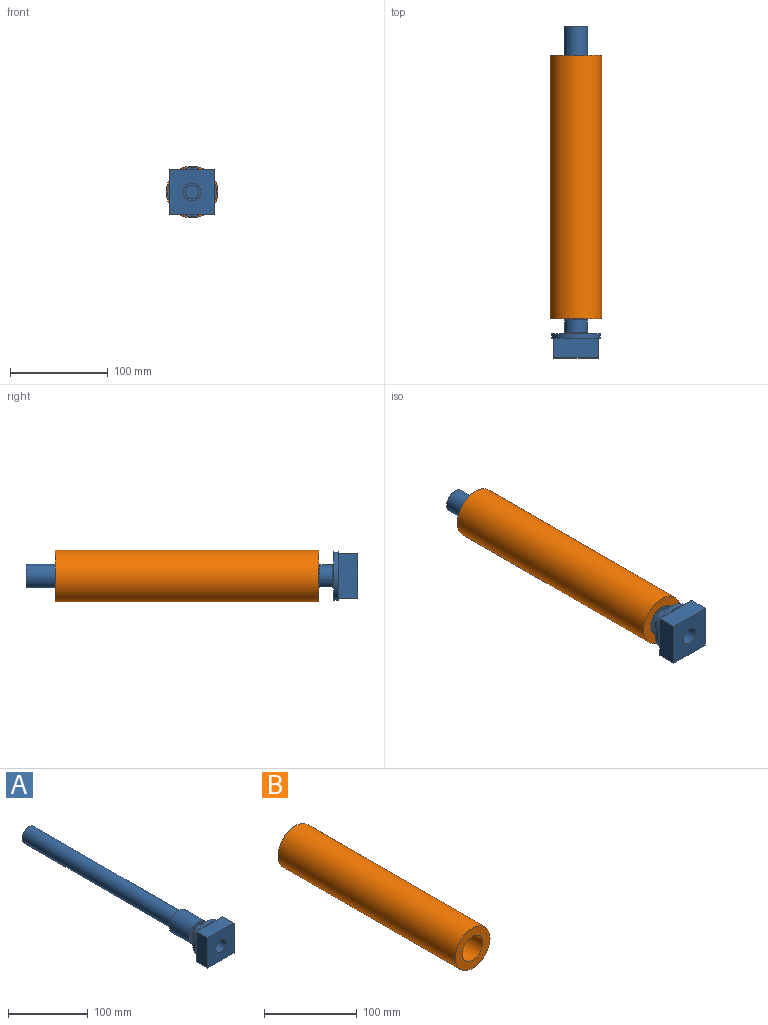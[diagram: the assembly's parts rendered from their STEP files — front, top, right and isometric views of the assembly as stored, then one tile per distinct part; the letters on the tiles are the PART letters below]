
ASSEMBLY  parts=2 mates=1
PART A: 27 faces, bbox 50x340x50 mm
  f0: plane 13.2x13.2mm, normal (0,1,0), area 64.5mm2, adj f5,f6,f12
  f1: plane 13.2x13.2mm, normal (0,1,0), area 64.5mm2, adj f4,f5,f12
  f2: plane 13.2x13.2mm, normal (0,1,0), area 64.5mm2, adj f3,f4,f12
  f3: plane 46x20mm, normal (0,0,-1), area 920mm2, adj f2,f4,f6,f7,f8,f9
  f4: plane 46x20mm, normal (1,0,0), area 920mm2, adj f1,f2,f3,f5,f7,f11
  f5: plane 46x20mm, normal (0,0,1), area 920mm2, adj f0,f1,f4,f6,f7,f14
  f6: plane 46x20mm, normal (-1,0,0), area 920mm2, adj f0,f3,f5,f7,f8,f10
  f7: plane 46x46mm, normal (0,-1,0), area 1847.2mm2, adj f3,f4,f5,f6,f23
  f8: plane 13.2x13.2mm, normal (0,1,0), area 64.5mm2, adj f3,f6,f12
  f9: plane 19.6x2mm, normal (0,-1,0), area 26.3mm2, adj f3,f12
  f10: plane 19.6x2mm, normal (0,-1,0), area 26.3mm2, adj f6,f12
  f11: plane 19.6x2mm, normal (0,-1,0), area 26.3mm2, adj f4,f12
  f12: cylinder r=25mm len=50mm, axis (0,-1,0), area 785.4mm2, adj f0,f1,f2,f8,f9,f10,f11,f13
  f13: plane 50x50mm, normal (0,1,0), area 1472.6mm2, adj f12,f16
  f14: plane 19.6x2mm, normal (0,-1,0), area 26.3mm2, adj f5,f12
  f15: cylinder r=11.5mm len=23mm, axis (0,-1,0), area 939.3mm2, adj f16,f20
  f16: torus R=12.5mm, axis (0,1,0), area 117.1mm2, adj f13,f15
  f17: cylinder r=16.5mm len=35mm, axis (0,-1,0), area 3628.5mm2, adj f18,f19
  f18: plane 33x33mm, normal (0,1,0), area 402.9mm2, adj f17,f21
  f19: plane 33x33mm, normal (0,-1,0), area 364.4mm2, adj f17,f20
  f20: torus R=12.5mm, axis (0,1,0), area 117.1mm2, adj f15,f19
  f21: cylinder r=12mm len=265mm, axis (0,-1,0), area 19980.5mm2, adj f18,f22
  f22: plane 24x24mm, normal (0,1,0), area 452.4mm2, adj f21
  f23: cylinder r=9.25mm len=20mm, axis (0,-1,0), area 1162.4mm2, adj f7,f24
  f24: plane 18.5x18.5mm, normal (0,-1,0), area 114.9mm2, adj f23,f25
  f25: cylinder r=7mm len=310mm, axis (0,-1,0), area 13634.5mm2, adj f24,f26
  f26: plane 14x14mm, normal (0,-1,0), area 153.9mm2, adj f25
PART B: 6 faces, bbox 53x270x53 mm
  f0: cylinder r=26.5mm len=270mm, axis (0,-1,0), area 44956.2mm2, adj f1,f2
  f1: plane 53x53mm, normal (0,1,0), area 1675.3mm2, adj f0,f5
  f2: plane 53x53mm, normal (0,-1,0), area 1451.4mm2, adj f0,f3
  f3: cylinder r=15.5mm len=35mm, axis (0,-1,0), area 3408.6mm2, adj f2,f4
  f4: plane 31x31mm, normal (0,-1,0), area 223.8mm2, adj f3,f5
  f5: cylinder r=13mm len=235mm, axis (0,-1,0), area 19195.1mm2, adj f1,f4
PLACE A t=(-72.29,-136.16,83.36)mm
PLACE B t=(-72.29,-116.16,83.36)mm fixed
MATE cylindrical A.f12 <-> B.f0  axis (0,-1,0) through (-72.29,-116.16,83.36)mm
